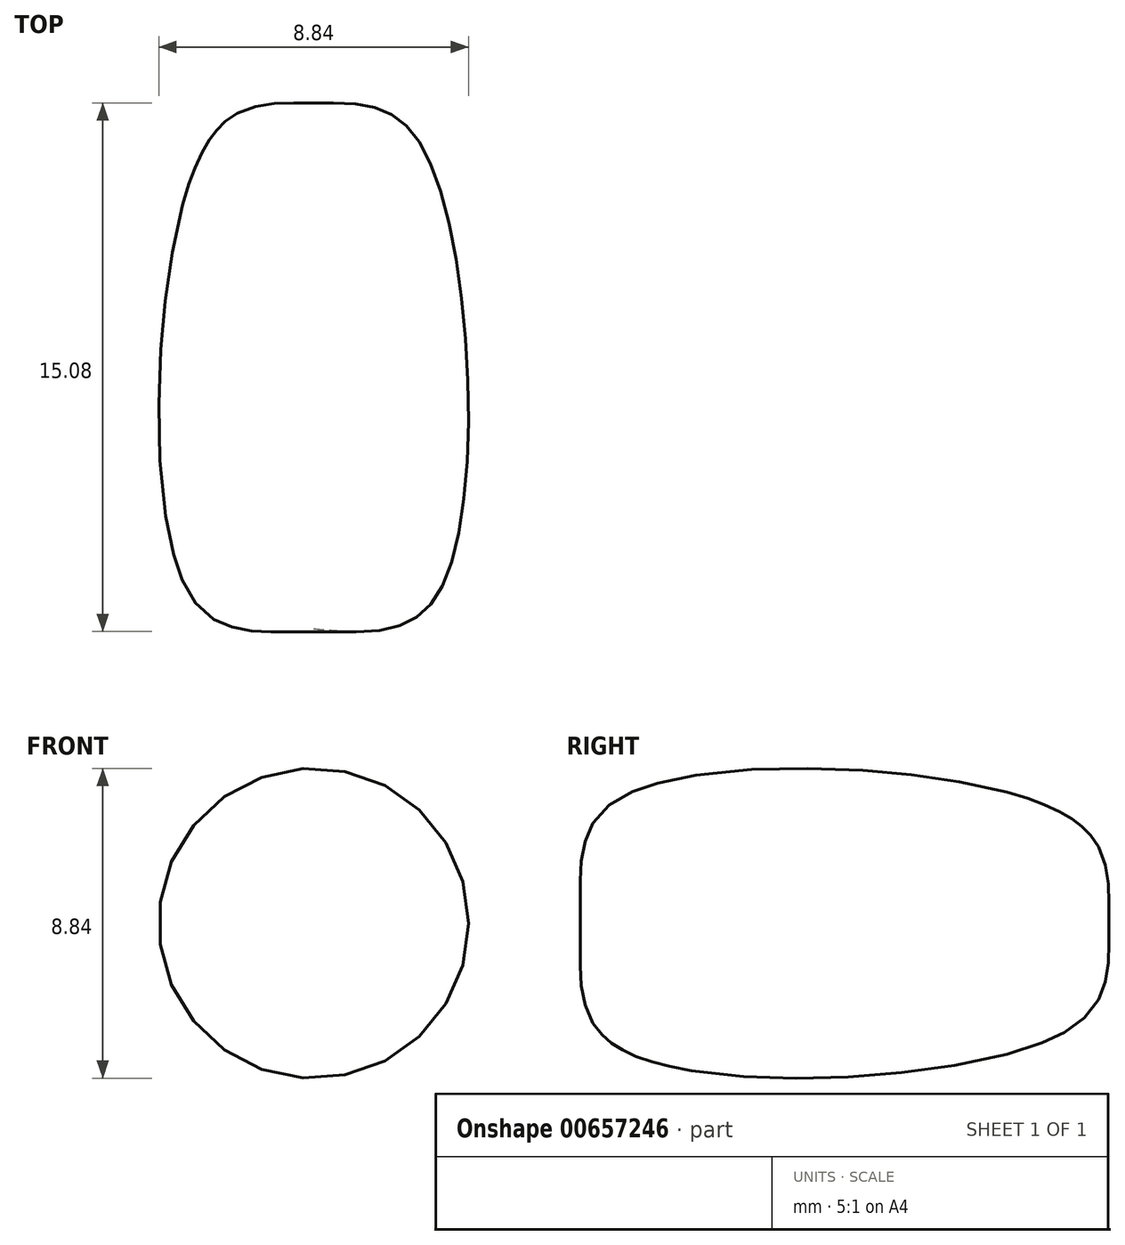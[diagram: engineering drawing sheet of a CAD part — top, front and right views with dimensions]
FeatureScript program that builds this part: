
annotation { "Feature Type Name" : "Feature", "Feature Type Description" : "" }
export const myFeature = defineFeature(function(context is Context, id is Id, definition is map)
    precondition{}
    {
        {
            var Q0;
            Q0=qCreatedBy(makeId("Top.planeOp"),FACE);
            var sketch = newSketch(context, id + "F0", { "sketchPlane" : qUnion([Q0])});
            skLineSegment(sketch, "E0", {"start": v(0, 0) * mm, "end": v(0, 15) * mm});
            skFitSpline(sketch, "E1", {"points": [v(0, 15) * mm, v(3.24, 13.5) * mm, v(3.8, 1.5) * mm, v(0, 0) * mm], "startDerivative": vector(18.9, 0.87) * mm, "endDerivative": vector(-22.5, 2.26) * mm});
            skLineSegment(sketch, "E2", {"start": v(24.38, 5.43) * mm, "end": v(24.38, 18.43) * mm});
            skFitSpline(sketch, "E3", {"points": [v(24.38, 18.43) * mm, v(26.77, 17.62) * mm, v(27.74, 7.37) * mm, v(24.38, 5.43) * mm], "startDerivative": vector(18.9, 0.87) * mm, "endDerivative": vector(-22.5, 2.26) * mm});
            skSolve(sketch);
        }
        {
            var Q0;
            Q0=makeQuery(id+"F0.imprint","IMPRINT",FACE,{"disambiguationData":[TD([[makeQuery(id+"F0.imprint","IMPRINT",EDGE,{"derivedFrom":sQuery(id+"F0.wireOp",EDGE,"E0")}),-1.0]])]});
            var Q1;
            Q1=sQuery(id+"F0.wireOp",EDGE,"E0");
            revolve(context, id + "F1", {"entities" : qUnion([Q0]), "axis" : qUnion([Q1]), "revolveType" : RevolveType.FULL});
        }
    });
